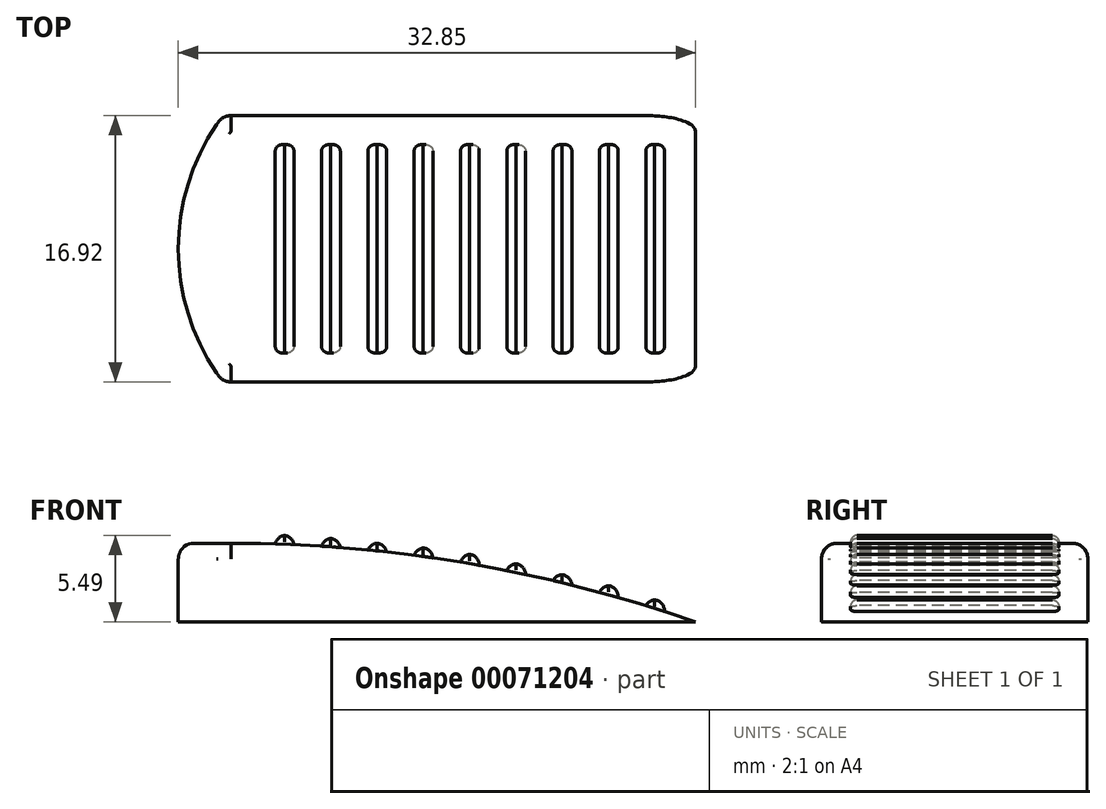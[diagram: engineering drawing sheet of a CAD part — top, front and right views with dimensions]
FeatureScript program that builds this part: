
annotation { "Feature Type Name" : "Feature", "Feature Type Description" : "" }
export const myFeature = defineFeature(function(context is Context, id is Id, definition is map)
    precondition{}
    {
        {
            var Q0;
            Q0=qCreatedBy(makeId("Top.planeOp"),FACE);
            var sketch = newSketch(context, id + "F0", { "sketchPlane" : qUnion([Q0])});
            skArc(sketch, "E0", {"start": v(11.65, 8.46) * mm, "mid": v(8.8, 0) * mm, "end": v(11.65, -8.46) * mm});
            skPoint(sketch, "E1.endSnap0", {"position": v(140.65, 0) * mm});
            skPoint(sketch, "E2.oppositeSnap0", {"position": v(24.14, -8.46) * mm});
            skLineSegment(sketch, "E2.bottom", {"start": v(11.65, 8.46) * mm, "end": v(41.65, 8.46) * mm});
            skLineSegment(sketch, "E2.top", {"start": v(11.65, -8.46) * mm, "end": v(41.65, -8.46) * mm});
            skLineSegment(sketch, "E2.right", {"start": v(41.65, 8.46) * mm, "end": v(41.65, -8.46) * mm});
            skSolve(sketch);
        }
        {
            var Q0;
            Q0=qSketchRegion(id+"F0",true);
            extrude(context, id + "F1", {"entities" : qUnion([Q0]), "depth" : 5 * mm});
        }
        {
            var Q0;
            Q0=makeQuery(id+"F1.opExtrude","CAP_EDGE",EDGE,{"disambiguationData":[OSD([sQuery(id+"F0.wireOp",EDGE,"E2.right")])],"isStart":false});
            fillet(context, id + "F2", {"entities" : qUnion([Q0]), "radius" : 90 * mm, "tangentPropagation" : true, "allowEdgeOverflow" : false});
        }
        {
            var Q0;
            Q0=makeQuery(id+"F2.opFillet","BLEND_EDGE",EDGE,{"blendedFrom":[makeQuery(id+"F1.opExtrude","CAP_EDGE",EDGE,{"disambiguationData":[OSD([sQuery(id+"F0.wireOp",EDGE,"E2.right")])],"isStart":false}),makeQuery(id+"F1.opExtrude","SWEPT_FACE",FACE,{"disambiguationData":[OSD([sQuery(id+"F0.wireOp",EDGE,"E2.top")])]})],"blendedInto":[makeQuery(id+"F1.opExtrude","SWEPT_FACE",FACE,{"disambiguationData":[OSD([sQuery(id+"F0.wireOp",EDGE,"E2.top")])]})]});
            var Q1;
            Q1=makeQuery(id+"F2.opFillet","BLEND_EDGE",EDGE,{"blendedFrom":[makeQuery(id+"F1.opExtrude","CAP_EDGE",EDGE,{"disambiguationData":[OSD([sQuery(id+"F0.wireOp",EDGE,"E2.right")])],"isStart":false}),makeQuery(id+"F1.opExtrude","SWEPT_FACE",FACE,{"disambiguationData":[OSD([sQuery(id+"F0.wireOp",EDGE,"E2.bottom")])]})],"blendedInto":[makeQuery(id+"F1.opExtrude","SWEPT_FACE",FACE,{"disambiguationData":[OSD([sQuery(id+"F0.wireOp",EDGE,"E2.bottom")])]})]});
            var Q2;
            Q2=makeQuery(id+"F1.opExtrude","CAP_EDGE",EDGE,{"disambiguationData":[OSD([sQuery(id+"F0.wireOp",EDGE,"E0")])],"isStart":false});
            fillet(context, id + "F3", {"entities" : qUnion([Q0, Q1, Q2]), "radius" : 1 * mm, "tangentPropagation" : true, "allowEdgeOverflow" : false});
        }
        {
            var Q0;
            Q0=makeQuery(id+"F1.opExtrude","SWEPT_EDGE",EDGE,{"disambiguationData":[OSD([sQuery(id+"F0.wireOp",EDGE,"E0"),sQuery(id+"F0.wireOp",EDGE,"E2.bottom")])]});
            var Q1;
            Q1=makeQuery(id+"F1.opExtrude","SWEPT_EDGE",EDGE,{"disambiguationData":[OSD([sQuery(id+"F0.wireOp",EDGE,"E0"),sQuery(id+"F0.wireOp",EDGE,"E2.top")])]});
            fillet(context, id + "F4", {"entities" : qUnion([Q0, Q1]), "radius" : 1 * mm, "tangentPropagation" : true, "allowEdgeOverflow" : false});
        }
        {
            var Q0;
            Q0=makeQuery(id+"F1.opExtrude","CAP_FACE",FACE,{"disambiguationData":[OSD([sQuery(id+"F0.wireOp",EDGE,"E0"),sQuery(id+"F0.wireOp",EDGE,"E2.bottom"),sQuery(id+"F0.wireOp",EDGE,"E2.top"),sQuery(id+"F0.wireOp",EDGE,"E2.right")])],"isStart":true});
            var sketch = newSketch(context, id + "F5", { "sketchPlane" : qUnion([Q0])});
            skPoint(sketch, "E3.rect.middle", {"position": v(27.32, 0) * mm});
            skPoint(sketch, "E4.startSnap0", {"position": v(21.43, 0) * mm});
            skPoint(sketch, "E5.startSnap0", {"position": v(18.5, 0) * mm});
            skPoint(sketch, "E6.rect.middle", {"position": v(15.55, 0) * mm});
            skLineSegment(sketch, "E7.rect.bottom", {"start": v(16.15, 6.61) * mm, "end": v(14.96, 6.61) * mm});
            skLineSegment(sketch, "E7.rect.top", {"start": v(16.15, -6.61) * mm, "end": v(14.96, -6.61) * mm});
            skLineSegment(sketch, "E7.rect.left", {"start": v(16.15, 6.61) * mm, "end": v(16.15, -6.61) * mm});
            skLineSegment(sketch, "E7.rect.right", {"start": v(14.96, 6.61) * mm, "end": v(14.96, -6.61) * mm});
            skLineSegment(sketch, "E8.MirrorCS", {"start": v(20.84, 6.61) * mm, "end": v(20.84, -6.61) * mm});
            skLineSegment(sketch, "E9.MirrorCS", {"start": v(22.03, 6.61) * mm, "end": v(22.03, -6.61) * mm});
            skLineSegment(sketch, "E10.MirrorCS", {"start": v(20.84, 6.61) * mm, "end": v(22.03, 6.61) * mm});
            skLineSegment(sketch, "E11.MirrorCS", {"start": v(20.84, -6.61) * mm, "end": v(22.03, -6.61) * mm});
            skLineSegment(sketch, "E12.MirrorCS", {"start": v(17.9, 6.61) * mm, "end": v(17.9, -6.61) * mm});
            skLineSegment(sketch, "E13.MirrorCS", {"start": v(19.09, 6.61) * mm, "end": v(19.09, -6.61) * mm});
            skLineSegment(sketch, "E14.MirrorCS", {"start": v(17.9, 6.61) * mm, "end": v(19.09, 6.61) * mm});
            skLineSegment(sketch, "E15.MirrorCS", {"start": v(17.9, -6.61) * mm, "end": v(19.09, -6.61) * mm});
            skLineSegment(sketch, "E16.MirrorCS", {"start": v(23.78, 6.61) * mm, "end": v(23.78, -6.61) * mm});
            skLineSegment(sketch, "E17.MirrorCS", {"start": v(24.97, 6.61) * mm, "end": v(24.97, -6.61) * mm});
            skLineSegment(sketch, "E18.MirrorCS", {"start": v(26.72, 6.61) * mm, "end": v(26.72, -6.61) * mm});
            skLineSegment(sketch, "E19.MirrorCS", {"start": v(27.91, 6.61) * mm, "end": v(27.91, -6.61) * mm});
            skLineSegment(sketch, "E20.MirrorCS", {"start": v(26.72, 6.61) * mm, "end": v(27.91, 6.61) * mm});
            skLineSegment(sketch, "E21.MirrorCS", {"start": v(26.72, -6.61) * mm, "end": v(27.91, -6.61) * mm});
            skLineSegment(sketch, "E22.MirrorCS", {"start": v(24.97, -6.61) * mm, "end": v(23.78, -6.61) * mm});
            skLineSegment(sketch, "E23.MirrorCS", {"start": v(24.97, 6.61) * mm, "end": v(23.78, 6.61) * mm});
            skLineSegment(sketch, "E24.MirrorCS", {"start": v(29.66, 6.61) * mm, "end": v(29.66, -6.61) * mm});
            skLineSegment(sketch, "E25.MirrorCS", {"start": v(30.85, 6.61) * mm, "end": v(30.85, -6.61) * mm});
            skLineSegment(sketch, "E26.MirrorCS", {"start": v(32.6, 6.61) * mm, "end": v(32.6, -6.61) * mm});
            skLineSegment(sketch, "E27.MirrorCS", {"start": v(33.8, 6.61) * mm, "end": v(33.8, -6.61) * mm});
            skLineSegment(sketch, "E28.MirrorCS", {"start": v(35.55, 6.61) * mm, "end": v(35.55, -6.61) * mm});
            skLineSegment(sketch, "E29.MirrorCS", {"start": v(36.74, 6.61) * mm, "end": v(36.74, -6.61) * mm});
            skLineSegment(sketch, "E30.MirrorCS", {"start": v(38.49, 6.61) * mm, "end": v(38.49, -6.61) * mm});
            skLineSegment(sketch, "E31.MirrorCS", {"start": v(39.68, 6.61) * mm, "end": v(39.68, -6.61) * mm});
            skLineSegment(sketch, "E32", {"start": v(29.66, 6.61) * mm, "end": v(30.85, 6.61) * mm});
            skLineSegment(sketch, "E33", {"start": v(32.6, 6.61) * mm, "end": v(33.8, 6.61) * mm});
            skLineSegment(sketch, "E34", {"start": v(35.55, 6.61) * mm, "end": v(36.74, 6.61) * mm});
            skLineSegment(sketch, "E35", {"start": v(38.49, 6.61) * mm, "end": v(39.68, 6.61) * mm});
            skLineSegment(sketch, "E36", {"start": v(39.68, -6.61) * mm, "end": v(38.49, -6.61) * mm});
            skLineSegment(sketch, "E37", {"start": v(36.74, -6.61) * mm, "end": v(35.55, -6.61) * mm});
            skLineSegment(sketch, "E38", {"start": v(33.8, -6.61) * mm, "end": v(32.6, -6.61) * mm});
            skLineSegment(sketch, "E39", {"start": v(30.85, -6.61) * mm, "end": v(29.66, -6.61) * mm});
            skSolve(sketch);
        }
        {
            var Q0;
            Q0=makeQuery(id+"F5.imprint","IMPRINT",FACE,{"disambiguationData":[TD([[makeQuery(id+"F5.imprint","IMPRINT",EDGE,{"derivedFrom":sQuery(id+"F5.wireOp",EDGE,"E7.rect.bottom")}),1.0]])]});
            extrude(context, id + "F6", {"entities" : qUnion([Q0]), "operationType" : NewBodyOperationType.ADD, "oppositeDirection" : true, "depth" : 5.5 * mm});
        }
        {
            var Q0;
            Q0=makeQuery(id+"F6.opExtrude","CAP_EDGE",EDGE,{"disambiguationData":[OSD([sQuery(id+"F5.wireOp",EDGE,"E7.rect.left")])],"isStart":false});
            var Q1;
            Q1=makeQuery(id+"F6.opExtrude","CAP_EDGE",EDGE,{"disambiguationData":[OSD([sQuery(id+"F5.wireOp",EDGE,"E7.rect.right")])],"isStart":false});
            fillet(context, id + "F7", {"entities" : qUnion([Q0, Q1]), "radius" : 0.7 * mm, "tangentPropagation" : true, "allowEdgeOverflow" : false});
        }
        {
            var Q0;
            Q0=makeQuery(id+"F5.imprint","IMPRINT",FACE,{"disambiguationData":[TD([[makeQuery(id+"F5.imprint","IMPRINT",EDGE,{"derivedFrom":sQuery(id+"F5.wireOp",EDGE,"E7.rect.bottom")}),-1.0]])]});
            var sketch = newSketch(context, id + "F8", { "sketchPlane" : qUnion([Q0])});
            skLineSegment(sketch, "E40.bottom", {"start": v(24.97, 6.61) * mm, "end": v(23.78, 6.61) * mm});
            skLineSegment(sketch, "E40.top", {"start": v(24.97, -6.61) * mm, "end": v(23.78, -6.61) * mm});
            skLineSegment(sketch, "E40.left", {"start": v(24.97, 6.61) * mm, "end": v(24.97, -6.61) * mm});
            skLineSegment(sketch, "E40.right", {"start": v(23.78, 6.61) * mm, "end": v(23.78, -6.61) * mm});
            skSolve(sketch);
        }
        {
            var Q0;
            Q0 = qSketchRegion(id + "F8", true);
            extrude(context, id + "F9", {"entities" : qUnion([Q0]), "operationType" : NewBodyOperationType.ADD, "oppositeDirection" : true, "depth" : 4.7 * mm});
        }
        {
            var Q0;
            Q0=makeQuery(id+"F9.opExtrude","CAP_EDGE",EDGE,{"disambiguationData":[OSD([sQuery(id+"F8.wireOp",EDGE,"E40.left")])],"isStart":false});
            var Q1;
            Q1=makeQuery(id+"F9.opExtrude","CAP_EDGE",EDGE,{"disambiguationData":[OSD([sQuery(id+"F8.wireOp",EDGE,"E40.right")])],"isStart":false});
            fillet(context, id + "F10", {"entities" : qUnion([Q0, Q1]), "radius" : 0.7 * mm, "tangentPropagation" : true, "allowEdgeOverflow" : false});
        }
        {
            var Q0;
            Q0=makeQuery(id+"F0.imprint","IMPRINT",FACE,{"disambiguationData":[TD([[makeQuery(id+"F0.imprint","IMPRINT",EDGE,{"derivedFrom":sQuery(id+"F0.wireOp",EDGE,"E0")}),1.0]])]});
            var sketch = newSketch(context, id + "F11", { "sketchPlane" : qUnion([Q0])});
            skLineSegment(sketch, "E41.bottom", {"start": v(33.8, -6.61) * mm, "end": v(32.6, -6.61) * mm});
            skLineSegment(sketch, "E41.top", {"start": v(33.8, 6.61) * mm, "end": v(32.6, 6.61) * mm});
            skLineSegment(sketch, "E41.left", {"start": v(33.8, -6.61) * mm, "end": v(33.8, 6.61) * mm});
            skLineSegment(sketch, "E41.right", {"start": v(32.6, -6.61) * mm, "end": v(32.6, 6.61) * mm});
            skSolve(sketch);
        }
        {
            var Q0;
            Q0=makeQuery(id+"F11.imprint","IMPRINT",FACE,{"disambiguationData":[TD([[makeQuery(id+"F11.imprint","IMPRINT",EDGE,{"derivedFrom":sQuery(id+"F11.wireOp",EDGE,"E41.bottom")}),-1.0]])]});
            extrude(context, id + "F12", {"entities" : qUnion([Q0]), "operationType" : NewBodyOperationType.ADD, "depth" : 3 * mm});
        }
        {
            var Q0;
            Q0=makeQuery(id+"F12.opExtrude","CAP_EDGE",EDGE,{"disambiguationData":[OSD([sQuery(id+"F11.wireOp",EDGE,"E41.left")])],"isStart":false});
            var Q1;
            Q1=makeQuery(id+"F12.opExtrude","CAP_EDGE",EDGE,{"disambiguationData":[OSD([sQuery(id+"F11.wireOp",EDGE,"E41.right")])],"isStart":false});
            fillet(context, id + "F13", {"entities" : qUnion([Q0, Q1]), "radius" : 0.7 * mm, "tangentPropagation" : true, "allowEdgeOverflow" : false});
        }
        {
            var Q0;
            Q0=makeQuery(id+"F5.imprint","IMPRINT",FACE,{"disambiguationData":[TD([[makeQuery(id+"F5.imprint","IMPRINT",EDGE,{"derivedFrom":sQuery(id+"F5.wireOp",EDGE,"E7.rect.bottom")}),-1.0]])]});
            var sketch = newSketch(context, id + "F14", { "sketchPlane" : qUnion([Q0])});
            skLineSegment(sketch, "E42.bottom", {"start": v(39.68, 6.61) * mm, "end": v(38.49, 6.61) * mm});
            skLineSegment(sketch, "E42.top", {"start": v(39.68, -6.61) * mm, "end": v(38.49, -6.61) * mm});
            skLineSegment(sketch, "E42.left", {"start": v(39.68, 6.61) * mm, "end": v(39.68, -6.61) * mm});
            skLineSegment(sketch, "E42.right", {"start": v(38.49, 6.61) * mm, "end": v(38.49, -6.61) * mm});
            skSolve(sketch);
        }
        {
            var Q0;
            Q0 = qSketchRegion(id + "F14", true);
            extrude(context, id + "F15", {"entities" : qUnion([Q0]), "operationType" : NewBodyOperationType.ADD, "oppositeDirection" : true, "depth" : 1.4 * mm});
        }
        {
            var Q0;
            Q0=makeQuery(id+"F15.opExtrude","CAP_EDGE",EDGE,{"disambiguationData":[OSD([sQuery(id+"F14.wireOp",EDGE,"E42.right")])],"isStart":false});
            var Q1;
            Q1=makeQuery(id+"F15.opExtrude","CAP_EDGE",EDGE,{"disambiguationData":[OSD([sQuery(id+"F14.wireOp",EDGE,"E42.left")])],"isStart":false});
            fillet(context, id + "F16", {"entities" : qUnion([Q0, Q1]), "radius" : 0.7 * mm, "tangentPropagation" : true, "allowEdgeOverflow" : false});
        }
        {
            var Q0;
            Q0=makeQuery(id+"F0.imprint","IMPRINT",FACE,{"disambiguationData":[TD([[makeQuery(id+"F0.imprint","IMPRINT",EDGE,{"derivedFrom":sQuery(id+"F0.wireOp",EDGE,"E0")}),1.0]])]});
            var sketch = newSketch(context, id + "F17", { "sketchPlane" : qUnion([Q0])});
            skLineSegment(sketch, "E43.bottom", {"start": v(35.55, -6.61) * mm, "end": v(36.74, -6.61) * mm});
            skLineSegment(sketch, "E43.top", {"start": v(35.55, 6.61) * mm, "end": v(36.74, 6.61) * mm});
            skLineSegment(sketch, "E43.left", {"start": v(35.55, -6.61) * mm, "end": v(35.55, 6.61) * mm});
            skLineSegment(sketch, "E43.right", {"start": v(36.74, -6.61) * mm, "end": v(36.74, 6.61) * mm});
            skSolve(sketch);
        }
        {
            var Q0;
            Q0 = qSketchRegion(id + "F17", true);
            extrude(context, id + "F18", {"entities" : qUnion([Q0]), "operationType" : NewBodyOperationType.ADD, "depth" : 2.3 * mm});
        }
        {
            var Q0;
            Q0=makeQuery(id+"F18.opExtrude","CAP_EDGE",EDGE,{"disambiguationData":[OSD([sQuery(id+"F17.wireOp",EDGE,"E43.left")])],"isStart":false});
            var Q1;
            Q1=makeQuery(id+"F18.opExtrude","CAP_EDGE",EDGE,{"disambiguationData":[OSD([sQuery(id+"F17.wireOp",EDGE,"E43.right")])],"isStart":false});
            fillet(context, id + "F19", {"entities" : qUnion([Q0, Q1]), "radius" : 0.7 * mm, "tangentPropagation" : true, "allowEdgeOverflow" : false});
        }
        {
            var Q0;
            Q0=makeQuery(id+"F0.imprint","IMPRINT",FACE,{"disambiguationData":[TD([[makeQuery(id+"F0.imprint","IMPRINT",EDGE,{"derivedFrom":sQuery(id+"F0.wireOp",EDGE,"E0")}),1.0]])]});
            var sketch = newSketch(context, id + "F20", { "sketchPlane" : qUnion([Q0])});
            skLineSegment(sketch, "E44.bottom", {"start": v(30.85, -6.61) * mm, "end": v(29.66, -6.61) * mm});
            skLineSegment(sketch, "E44.top", {"start": v(30.85, 6.61) * mm, "end": v(29.66, 6.61) * mm});
            skLineSegment(sketch, "E44.left", {"start": v(30.85, -6.61) * mm, "end": v(30.85, 6.61) * mm});
            skLineSegment(sketch, "E44.right", {"start": v(29.66, -6.61) * mm, "end": v(29.66, 6.61) * mm});
            skSolve(sketch);
        }
        {
            var Q0;
            Q0 = qSketchRegion(id + "F20", true);
            extrude(context, id + "F21", {"entities" : qUnion([Q0]), "operationType" : NewBodyOperationType.ADD, "depth" : 3.7 * mm});
        }
        {
            var Q0;
            Q0=makeQuery(id+"F21.opExtrude","CAP_EDGE",EDGE,{"disambiguationData":[OSD([sQuery(id+"F20.wireOp",EDGE,"E44.right")])],"isStart":false});
            var Q1;
            Q1=makeQuery(id+"F21.opExtrude","CAP_EDGE",EDGE,{"disambiguationData":[OSD([sQuery(id+"F20.wireOp",EDGE,"E44.left")])],"isStart":false});
            fillet(context, id + "F22", {"entities" : qUnion([Q0, Q1]), "radius" : 0.7 * mm, "tangentPropagation" : true, "allowEdgeOverflow" : false});
        }
        {
            var Q0;
            Q0=makeQuery(id+"F0.imprint","IMPRINT",FACE,{"disambiguationData":[TD([[makeQuery(id+"F0.imprint","IMPRINT",EDGE,{"derivedFrom":sQuery(id+"F0.wireOp",EDGE,"E0")}),1.0]])]});
            var sketch = newSketch(context, id + "F23", { "sketchPlane" : qUnion([Q0])});
            skLineSegment(sketch, "E45.bottom", {"start": v(27.91, -6.61) * mm, "end": v(26.72, -6.61) * mm});
            skLineSegment(sketch, "E45.top", {"start": v(27.91, 6.61) * mm, "end": v(26.72, 6.61) * mm});
            skLineSegment(sketch, "E45.left", {"start": v(27.91, -6.61) * mm, "end": v(27.91, 6.61) * mm});
            skLineSegment(sketch, "E45.right", {"start": v(26.72, -6.61) * mm, "end": v(26.72, 6.61) * mm});
            skSolve(sketch);
        }
        {
            var Q0;
            Q0 = qSketchRegion(id + "F23", true);
            extrude(context, id + "F24", {"entities" : qUnion([Q0]), "operationType" : NewBodyOperationType.ADD, "depth" : 4.3 * mm});
        }
        {
            var Q0;
            Q0=makeQuery(id+"F24.opExtrude","CAP_EDGE",EDGE,{"disambiguationData":[OSD([sQuery(id+"F23.wireOp",EDGE,"E45.right")])],"isStart":false});
            var Q1;
            Q1=makeQuery(id+"F24.opExtrude","CAP_EDGE",EDGE,{"disambiguationData":[OSD([sQuery(id+"F23.wireOp",EDGE,"E45.left")])],"isStart":false});
            fillet(context, id + "F25", {"entities" : qUnion([Q0, Q1]), "radius" : 0.7 * mm, "tangentPropagation" : true, "allowEdgeOverflow" : false});
        }
        {
            var Q0;
            Q0=makeQuery(id+"F5.imprint","IMPRINT",FACE,{"disambiguationData":[TD([[makeQuery(id+"F5.imprint","IMPRINT",EDGE,{"derivedFrom":sQuery(id+"F5.wireOp",EDGE,"E7.rect.bottom")}),-1.0]])]});
            var sketch = newSketch(context, id + "F26", { "sketchPlane" : qUnion([Q0])});
            skLineSegment(sketch, "E46.bottom", {"start": v(17.9, 6.61) * mm, "end": v(19.09, 6.61) * mm});
            skLineSegment(sketch, "E46.top", {"start": v(17.9, -6.61) * mm, "end": v(19.09, -6.61) * mm});
            skLineSegment(sketch, "E46.left", {"start": v(17.9, 6.61) * mm, "end": v(17.9, -6.61) * mm});
            skLineSegment(sketch, "E46.right", {"start": v(19.09, 6.61) * mm, "end": v(19.09, -6.61) * mm});
            skSolve(sketch);
        }
        {
            var Q0;
            Q0 = qSketchRegion(id + "F26", true);
            extrude(context, id + "F27", {"entities" : qUnion([Q0]), "operationType" : NewBodyOperationType.ADD, "oppositeDirection" : true, "depth" : 5.3 * mm});
        }
        {
            var Q0;
            Q0=makeQuery(id+"F27.opExtrude","CAP_EDGE",EDGE,{"disambiguationData":[OSD([sQuery(id+"F26.wireOp",EDGE,"E46.left")])],"isStart":false});
            var Q1;
            Q1=makeQuery(id+"F27.opExtrude","CAP_EDGE",EDGE,{"disambiguationData":[OSD([sQuery(id+"F26.wireOp",EDGE,"E46.right")])],"isStart":false});
            fillet(context, id + "F28", {"entities" : qUnion([Q0, Q1]), "radius" : 0.7 * mm, "tangentPropagation" : true, "allowEdgeOverflow" : false});
        }
        {
            var Q0;
            Q0=makeQuery(id+"F0.imprint","IMPRINT",FACE,{"disambiguationData":[TD([[makeQuery(id+"F0.imprint","IMPRINT",EDGE,{"derivedFrom":sQuery(id+"F0.wireOp",EDGE,"E0")}),1.0]])]});
            var sketch = newSketch(context, id + "F29", { "sketchPlane" : qUnion([Q0])});
            skLineSegment(sketch, "E47.bottom", {"start": v(22.03, -6.61) * mm, "end": v(20.84, -6.61) * mm});
            skLineSegment(sketch, "E47.top", {"start": v(22.03, 6.61) * mm, "end": v(20.84, 6.61) * mm});
            skLineSegment(sketch, "E47.left", {"start": v(22.03, -6.61) * mm, "end": v(22.03, 6.61) * mm});
            skLineSegment(sketch, "E47.right", {"start": v(20.84, -6.61) * mm, "end": v(20.84, 6.61) * mm});
            skSolve(sketch);
        }
        {
            var Q0;
            Q0 = qSketchRegion(id + "F29", true);
            extrude(context, id + "F30", {"entities" : qUnion([Q0]), "operationType" : NewBodyOperationType.ADD, "depth" : 5 * mm});
        }
        {
            var Q0;
            Q0=makeQuery(id+"F30.opExtrude","CAP_EDGE",EDGE,{"disambiguationData":[OSD([sQuery(id+"F29.wireOp",EDGE,"E47.right")])],"isStart":false});
            var Q1;
            Q1=makeQuery(id+"F30.opExtrude","CAP_EDGE",EDGE,{"disambiguationData":[OSD([sQuery(id+"F29.wireOp",EDGE,"E47.left")])],"isStart":false});
            fillet(context, id + "F31", {"entities" : qUnion([Q0, Q1]), "radius" : 0.7 * mm, "tangentPropagation" : true, "allowEdgeOverflow" : false});
        }
        {
            var Q0;
            Q0=makeQuery(id+"F7.opFillet","BLEND_EDGE",EDGE,{"blendedFrom":[makeQuery(id+"F6.opExtrude","CAP_EDGE",EDGE,{"disambiguationData":[OSD([sQuery(id+"F5.wireOp",EDGE,"E7.rect.left")])],"isStart":false}),makeQuery(id+"F6.opExtrude","SWEPT_FACE",FACE,{"disambiguationData":[OSD([sQuery(id+"F5.wireOp",EDGE,"E7.rect.bottom")])]})],"blendedInto":[makeQuery(id+"F6.opExtrude","SWEPT_FACE",FACE,{"disambiguationData":[OSD([sQuery(id+"F5.wireOp",EDGE,"E7.rect.bottom")])]})]});
            var Q1;
            Q1=makeQuery(id+"F7.opFillet","BLEND_EDGE",EDGE,{"blendedFrom":[makeQuery(id+"F6.opExtrude","CAP_EDGE",EDGE,{"disambiguationData":[OSD([sQuery(id+"F5.wireOp",EDGE,"E7.rect.right")])],"isStart":false}),makeQuery(id+"F6.opExtrude","SWEPT_FACE",FACE,{"disambiguationData":[OSD([sQuery(id+"F5.wireOp",EDGE,"E7.rect.bottom")])]})],"blendedInto":[makeQuery(id+"F6.opExtrude","SWEPT_FACE",FACE,{"disambiguationData":[OSD([sQuery(id+"F5.wireOp",EDGE,"E7.rect.bottom")])]})]});
            var Q2;
            Q2=makeQuery(id+"F28.opFillet","BLEND_EDGE",EDGE,{"blendedFrom":[makeQuery(id+"F27.opExtrude","CAP_EDGE",EDGE,{"disambiguationData":[OSD([sQuery(id+"F26.wireOp",EDGE,"E46.left")])],"isStart":false}),makeQuery(id+"F27.opExtrude","SWEPT_FACE",FACE,{"disambiguationData":[OSD([sQuery(id+"F26.wireOp",EDGE,"E46.bottom")])]})],"blendedInto":[makeQuery(id+"F27.opExtrude","SWEPT_FACE",FACE,{"disambiguationData":[OSD([sQuery(id+"F26.wireOp",EDGE,"E46.bottom")])]})]});
            var Q3;
            Q3=makeQuery(id+"F28.opFillet","BLEND_EDGE",EDGE,{"blendedFrom":[makeQuery(id+"F27.opExtrude","CAP_EDGE",EDGE,{"disambiguationData":[OSD([sQuery(id+"F26.wireOp",EDGE,"E46.right")])],"isStart":false}),makeQuery(id+"F27.opExtrude","SWEPT_FACE",FACE,{"disambiguationData":[OSD([sQuery(id+"F26.wireOp",EDGE,"E46.bottom")])]})],"blendedInto":[makeQuery(id+"F27.opExtrude","SWEPT_FACE",FACE,{"disambiguationData":[OSD([sQuery(id+"F26.wireOp",EDGE,"E46.bottom")])]})]});
            var Q4;
            Q4=makeQuery(id+"F31.opFillet","BLEND_EDGE",EDGE,{"blendedFrom":[makeQuery(id+"F30.opExtrude","CAP_EDGE",EDGE,{"disambiguationData":[OSD([sQuery(id+"F29.wireOp",EDGE,"E47.right")])],"isStart":false}),makeQuery(id+"F30.opExtrude","SWEPT_FACE",FACE,{"disambiguationData":[OSD([sQuery(id+"F29.wireOp",EDGE,"E47.bottom")])]})],"blendedInto":[makeQuery(id+"F30.opExtrude","SWEPT_FACE",FACE,{"disambiguationData":[OSD([sQuery(id+"F29.wireOp",EDGE,"E47.bottom")])]})]});
            var Q5;
            Q5=makeQuery(id+"F31.opFillet","BLEND_EDGE",EDGE,{"blendedFrom":[makeQuery(id+"F30.opExtrude","CAP_EDGE",EDGE,{"disambiguationData":[OSD([sQuery(id+"F29.wireOp",EDGE,"E47.left")])],"isStart":false}),makeQuery(id+"F30.opExtrude","SWEPT_FACE",FACE,{"disambiguationData":[OSD([sQuery(id+"F29.wireOp",EDGE,"E47.bottom")])]})],"blendedInto":[makeQuery(id+"F30.opExtrude","SWEPT_FACE",FACE,{"disambiguationData":[OSD([sQuery(id+"F29.wireOp",EDGE,"E47.bottom")])]})]});
            var Q6;
            Q6=makeQuery(id+"F10.opFillet","BLEND_EDGE",EDGE,{"blendedFrom":[makeQuery(id+"F9.opExtrude","CAP_EDGE",EDGE,{"disambiguationData":[OSD([sQuery(id+"F8.wireOp",EDGE,"E40.right")])],"isStart":false}),makeQuery(id+"F9.opExtrude","SWEPT_FACE",FACE,{"disambiguationData":[OSD([sQuery(id+"F8.wireOp",EDGE,"E40.bottom")])]})],"blendedInto":[makeQuery(id+"F9.opExtrude","SWEPT_FACE",FACE,{"disambiguationData":[OSD([sQuery(id+"F8.wireOp",EDGE,"E40.bottom")])]})]});
            var Q7;
            Q7=makeQuery(id+"F10.opFillet","BLEND_EDGE",EDGE,{"blendedFrom":[makeQuery(id+"F9.opExtrude","CAP_EDGE",EDGE,{"disambiguationData":[OSD([sQuery(id+"F8.wireOp",EDGE,"E40.left")])],"isStart":false}),makeQuery(id+"F9.opExtrude","SWEPT_FACE",FACE,{"disambiguationData":[OSD([sQuery(id+"F8.wireOp",EDGE,"E40.bottom")])]})],"blendedInto":[makeQuery(id+"F9.opExtrude","SWEPT_FACE",FACE,{"disambiguationData":[OSD([sQuery(id+"F8.wireOp",EDGE,"E40.bottom")])]})]});
            var Q8;
            Q8=makeQuery(id+"F25.opFillet","BLEND_EDGE",EDGE,{"blendedFrom":[makeQuery(id+"F24.opExtrude","CAP_EDGE",EDGE,{"disambiguationData":[OSD([sQuery(id+"F23.wireOp",EDGE,"E45.right")])],"isStart":false}),makeQuery(id+"F24.opExtrude","SWEPT_FACE",FACE,{"disambiguationData":[OSD([sQuery(id+"F23.wireOp",EDGE,"E45.bottom")])]})],"blendedInto":[makeQuery(id+"F24.opExtrude","SWEPT_FACE",FACE,{"disambiguationData":[OSD([sQuery(id+"F23.wireOp",EDGE,"E45.bottom")])]})]});
            var Q9;
            Q9=makeQuery(id+"F25.opFillet","BLEND_EDGE",EDGE,{"blendedFrom":[makeQuery(id+"F24.opExtrude","CAP_EDGE",EDGE,{"disambiguationData":[OSD([sQuery(id+"F23.wireOp",EDGE,"E45.left")])],"isStart":false}),makeQuery(id+"F24.opExtrude","SWEPT_FACE",FACE,{"disambiguationData":[OSD([sQuery(id+"F23.wireOp",EDGE,"E45.bottom")])]})],"blendedInto":[makeQuery(id+"F24.opExtrude","SWEPT_FACE",FACE,{"disambiguationData":[OSD([sQuery(id+"F23.wireOp",EDGE,"E45.bottom")])]})]});
            var Q10;
            Q10=makeQuery(id+"F22.opFillet","BLEND_EDGE",EDGE,{"blendedFrom":[makeQuery(id+"F21.opExtrude","CAP_EDGE",EDGE,{"disambiguationData":[OSD([sQuery(id+"F20.wireOp",EDGE,"E44.right")])],"isStart":false}),makeQuery(id+"F21.opExtrude","SWEPT_FACE",FACE,{"disambiguationData":[OSD([sQuery(id+"F20.wireOp",EDGE,"E44.bottom")])]})],"blendedInto":[makeQuery(id+"F21.opExtrude","SWEPT_FACE",FACE,{"disambiguationData":[OSD([sQuery(id+"F20.wireOp",EDGE,"E44.bottom")])]})]});
            var Q11;
            Q11=makeQuery(id+"F22.opFillet","BLEND_EDGE",EDGE,{"blendedFrom":[makeQuery(id+"F21.opExtrude","CAP_EDGE",EDGE,{"disambiguationData":[OSD([sQuery(id+"F20.wireOp",EDGE,"E44.left")])],"isStart":false}),makeQuery(id+"F21.opExtrude","SWEPT_FACE",FACE,{"disambiguationData":[OSD([sQuery(id+"F20.wireOp",EDGE,"E44.bottom")])]})],"blendedInto":[makeQuery(id+"F21.opExtrude","SWEPT_FACE",FACE,{"disambiguationData":[OSD([sQuery(id+"F20.wireOp",EDGE,"E44.bottom")])]})]});
            var Q12;
            Q12=makeQuery(id+"F13.opFillet","BLEND_EDGE",EDGE,{"blendedFrom":[makeQuery(id+"F12.opExtrude","CAP_EDGE",EDGE,{"disambiguationData":[OSD([sQuery(id+"F11.wireOp",EDGE,"E41.right")])],"isStart":false}),makeQuery(id+"F12.opExtrude","SWEPT_FACE",FACE,{"disambiguationData":[OSD([sQuery(id+"F11.wireOp",EDGE,"E41.bottom")])]})],"blendedInto":[makeQuery(id+"F12.opExtrude","SWEPT_FACE",FACE,{"disambiguationData":[OSD([sQuery(id+"F11.wireOp",EDGE,"E41.bottom")])]})]});
            var Q13;
            Q13=makeQuery(id+"F13.opFillet","BLEND_EDGE",EDGE,{"blendedFrom":[makeQuery(id+"F12.opExtrude","CAP_EDGE",EDGE,{"disambiguationData":[OSD([sQuery(id+"F11.wireOp",EDGE,"E41.left")])],"isStart":false}),makeQuery(id+"F12.opExtrude","SWEPT_FACE",FACE,{"disambiguationData":[OSD([sQuery(id+"F11.wireOp",EDGE,"E41.bottom")])]})],"blendedInto":[makeQuery(id+"F12.opExtrude","SWEPT_FACE",FACE,{"disambiguationData":[OSD([sQuery(id+"F11.wireOp",EDGE,"E41.bottom")])]})]});
            var Q14;
            Q14=makeQuery(id+"F19.opFillet","BLEND_EDGE",EDGE,{"blendedFrom":[makeQuery(id+"F18.opExtrude","CAP_EDGE",EDGE,{"disambiguationData":[OSD([sQuery(id+"F17.wireOp",EDGE,"E43.left")])],"isStart":false}),makeQuery(id+"F18.opExtrude","SWEPT_FACE",FACE,{"disambiguationData":[OSD([sQuery(id+"F17.wireOp",EDGE,"E43.bottom")])]})],"blendedInto":[makeQuery(id+"F18.opExtrude","SWEPT_FACE",FACE,{"disambiguationData":[OSD([sQuery(id+"F17.wireOp",EDGE,"E43.bottom")])]})]});
            var Q15;
            Q15=makeQuery(id+"F19.opFillet","BLEND_EDGE",EDGE,{"blendedFrom":[makeQuery(id+"F18.opExtrude","CAP_EDGE",EDGE,{"disambiguationData":[OSD([sQuery(id+"F17.wireOp",EDGE,"E43.right")])],"isStart":false}),makeQuery(id+"F18.opExtrude","SWEPT_FACE",FACE,{"disambiguationData":[OSD([sQuery(id+"F17.wireOp",EDGE,"E43.bottom")])]})],"blendedInto":[makeQuery(id+"F18.opExtrude","SWEPT_FACE",FACE,{"disambiguationData":[OSD([sQuery(id+"F17.wireOp",EDGE,"E43.bottom")])]})]});
            var Q16;
            Q16=makeQuery(id+"F16.opFillet","BLEND_EDGE",EDGE,{"blendedFrom":[makeQuery(id+"F15.opExtrude","CAP_EDGE",EDGE,{"disambiguationData":[OSD([sQuery(id+"F14.wireOp",EDGE,"E42.right")])],"isStart":false}),makeQuery(id+"F15.opExtrude","SWEPT_FACE",FACE,{"disambiguationData":[OSD([sQuery(id+"F14.wireOp",EDGE,"E42.bottom")])]})],"blendedInto":[makeQuery(id+"F15.opExtrude","SWEPT_FACE",FACE,{"disambiguationData":[OSD([sQuery(id+"F14.wireOp",EDGE,"E42.bottom")])]})]});
            var Q17;
            Q17=makeQuery(id+"F16.opFillet","BLEND_EDGE",EDGE,{"blendedFrom":[makeQuery(id+"F15.opExtrude","CAP_EDGE",EDGE,{"disambiguationData":[OSD([sQuery(id+"F14.wireOp",EDGE,"E42.left")])],"isStart":false}),makeQuery(id+"F15.opExtrude","SWEPT_FACE",FACE,{"disambiguationData":[OSD([sQuery(id+"F14.wireOp",EDGE,"E42.bottom")])]})],"blendedInto":[makeQuery(id+"F15.opExtrude","SWEPT_FACE",FACE,{"disambiguationData":[OSD([sQuery(id+"F14.wireOp",EDGE,"E42.bottom")])]})]});
            var Q18;
            Q18=makeQuery(id+"F16.opFillet","BLEND_EDGE",EDGE,{"blendedFrom":[makeQuery(id+"F15.opExtrude","CAP_EDGE",EDGE,{"disambiguationData":[OSD([sQuery(id+"F14.wireOp",EDGE,"E42.right")])],"isStart":false}),makeQuery(id+"F15.opExtrude","SWEPT_FACE",FACE,{"disambiguationData":[OSD([sQuery(id+"F14.wireOp",EDGE,"E42.top")])]})],"blendedInto":[makeQuery(id+"F15.opExtrude","SWEPT_FACE",FACE,{"disambiguationData":[OSD([sQuery(id+"F14.wireOp",EDGE,"E42.top")])]})]});
            var Q19;
            Q19=makeQuery(id+"F16.opFillet","BLEND_EDGE",EDGE,{"blendedFrom":[makeQuery(id+"F15.opExtrude","CAP_EDGE",EDGE,{"disambiguationData":[OSD([sQuery(id+"F14.wireOp",EDGE,"E42.left")])],"isStart":false}),makeQuery(id+"F15.opExtrude","SWEPT_FACE",FACE,{"disambiguationData":[OSD([sQuery(id+"F14.wireOp",EDGE,"E42.top")])]})],"blendedInto":[makeQuery(id+"F15.opExtrude","SWEPT_FACE",FACE,{"disambiguationData":[OSD([sQuery(id+"F14.wireOp",EDGE,"E42.top")])]})]});
            var Q20;
            Q20=makeQuery(id+"F19.opFillet","BLEND_EDGE",EDGE,{"blendedFrom":[makeQuery(id+"F18.opExtrude","CAP_EDGE",EDGE,{"disambiguationData":[OSD([sQuery(id+"F17.wireOp",EDGE,"E43.right")])],"isStart":false}),makeQuery(id+"F18.opExtrude","SWEPT_FACE",FACE,{"disambiguationData":[OSD([sQuery(id+"F17.wireOp",EDGE,"E43.top")])]})],"blendedInto":[makeQuery(id+"F18.opExtrude","SWEPT_FACE",FACE,{"disambiguationData":[OSD([sQuery(id+"F17.wireOp",EDGE,"E43.top")])]})]});
            var Q21;
            Q21=makeQuery(id+"F19.opFillet","BLEND_EDGE",EDGE,{"blendedFrom":[makeQuery(id+"F18.opExtrude","CAP_EDGE",EDGE,{"disambiguationData":[OSD([sQuery(id+"F17.wireOp",EDGE,"E43.left")])],"isStart":false}),makeQuery(id+"F18.opExtrude","SWEPT_FACE",FACE,{"disambiguationData":[OSD([sQuery(id+"F17.wireOp",EDGE,"E43.top")])]})],"blendedInto":[makeQuery(id+"F18.opExtrude","SWEPT_FACE",FACE,{"disambiguationData":[OSD([sQuery(id+"F17.wireOp",EDGE,"E43.top")])]})]});
            var Q22;
            Q22=makeQuery(id+"F7.opFillet","BLEND_EDGE",EDGE,{"blendedFrom":[makeQuery(id+"F6.opExtrude","CAP_EDGE",EDGE,{"disambiguationData":[OSD([sQuery(id+"F5.wireOp",EDGE,"E7.rect.right")])],"isStart":false}),makeQuery(id+"F6.opExtrude","SWEPT_FACE",FACE,{"disambiguationData":[OSD([sQuery(id+"F5.wireOp",EDGE,"E7.rect.top")])]})],"blendedInto":[makeQuery(id+"F6.opExtrude","SWEPT_FACE",FACE,{"disambiguationData":[OSD([sQuery(id+"F5.wireOp",EDGE,"E7.rect.top")])]})]});
            var Q23;
            Q23=makeQuery(id+"F7.opFillet","BLEND_EDGE",EDGE,{"blendedFrom":[makeQuery(id+"F6.opExtrude","CAP_EDGE",EDGE,{"disambiguationData":[OSD([sQuery(id+"F5.wireOp",EDGE,"E7.rect.left")])],"isStart":false}),makeQuery(id+"F6.opExtrude","SWEPT_FACE",FACE,{"disambiguationData":[OSD([sQuery(id+"F5.wireOp",EDGE,"E7.rect.top")])]})],"blendedInto":[makeQuery(id+"F6.opExtrude","SWEPT_FACE",FACE,{"disambiguationData":[OSD([sQuery(id+"F5.wireOp",EDGE,"E7.rect.top")])]})]});
            var Q24;
            Q24=makeQuery(id+"F28.opFillet","BLEND_EDGE",EDGE,{"blendedFrom":[makeQuery(id+"F27.opExtrude","CAP_EDGE",EDGE,{"disambiguationData":[OSD([sQuery(id+"F26.wireOp",EDGE,"E46.left")])],"isStart":false}),makeQuery(id+"F27.opExtrude","SWEPT_FACE",FACE,{"disambiguationData":[OSD([sQuery(id+"F26.wireOp",EDGE,"E46.top")])]})],"blendedInto":[makeQuery(id+"F27.opExtrude","SWEPT_FACE",FACE,{"disambiguationData":[OSD([sQuery(id+"F26.wireOp",EDGE,"E46.top")])]})]});
            var Q25;
            Q25=makeQuery(id+"F28.opFillet","BLEND_EDGE",EDGE,{"blendedFrom":[makeQuery(id+"F27.opExtrude","CAP_EDGE",EDGE,{"disambiguationData":[OSD([sQuery(id+"F26.wireOp",EDGE,"E46.right")])],"isStart":false}),makeQuery(id+"F27.opExtrude","SWEPT_FACE",FACE,{"disambiguationData":[OSD([sQuery(id+"F26.wireOp",EDGE,"E46.top")])]})],"blendedInto":[makeQuery(id+"F27.opExtrude","SWEPT_FACE",FACE,{"disambiguationData":[OSD([sQuery(id+"F26.wireOp",EDGE,"E46.top")])]})]});
            var Q26;
            Q26=makeQuery(id+"F31.opFillet","BLEND_EDGE",EDGE,{"blendedFrom":[makeQuery(id+"F30.opExtrude","CAP_EDGE",EDGE,{"disambiguationData":[OSD([sQuery(id+"F29.wireOp",EDGE,"E47.right")])],"isStart":false}),makeQuery(id+"F30.opExtrude","SWEPT_FACE",FACE,{"disambiguationData":[OSD([sQuery(id+"F29.wireOp",EDGE,"E47.top")])]})],"blendedInto":[makeQuery(id+"F30.opExtrude","SWEPT_FACE",FACE,{"disambiguationData":[OSD([sQuery(id+"F29.wireOp",EDGE,"E47.top")])]})]});
            var Q27;
            Q27=makeQuery(id+"F31.opFillet","BLEND_EDGE",EDGE,{"blendedFrom":[makeQuery(id+"F30.opExtrude","CAP_EDGE",EDGE,{"disambiguationData":[OSD([sQuery(id+"F29.wireOp",EDGE,"E47.left")])],"isStart":false}),makeQuery(id+"F30.opExtrude","SWEPT_FACE",FACE,{"disambiguationData":[OSD([sQuery(id+"F29.wireOp",EDGE,"E47.top")])]})],"blendedInto":[makeQuery(id+"F30.opExtrude","SWEPT_FACE",FACE,{"disambiguationData":[OSD([sQuery(id+"F29.wireOp",EDGE,"E47.top")])]})]});
            var Q28;
            Q28=makeQuery(id+"F10.opFillet","BLEND_EDGE",EDGE,{"blendedFrom":[makeQuery(id+"F9.opExtrude","CAP_EDGE",EDGE,{"disambiguationData":[OSD([sQuery(id+"F8.wireOp",EDGE,"E40.right")])],"isStart":false}),makeQuery(id+"F9.opExtrude","SWEPT_FACE",FACE,{"disambiguationData":[OSD([sQuery(id+"F8.wireOp",EDGE,"E40.top")])]})],"blendedInto":[makeQuery(id+"F9.opExtrude","SWEPT_FACE",FACE,{"disambiguationData":[OSD([sQuery(id+"F8.wireOp",EDGE,"E40.top")])]})]});
            var Q29;
            Q29=makeQuery(id+"F10.opFillet","BLEND_EDGE",EDGE,{"blendedFrom":[makeQuery(id+"F9.opExtrude","CAP_EDGE",EDGE,{"disambiguationData":[OSD([sQuery(id+"F8.wireOp",EDGE,"E40.left")])],"isStart":false}),makeQuery(id+"F9.opExtrude","SWEPT_FACE",FACE,{"disambiguationData":[OSD([sQuery(id+"F8.wireOp",EDGE,"E40.top")])]})],"blendedInto":[makeQuery(id+"F9.opExtrude","SWEPT_FACE",FACE,{"disambiguationData":[OSD([sQuery(id+"F8.wireOp",EDGE,"E40.top")])]})]});
            var Q30;
            Q30=makeQuery(id+"F25.opFillet","BLEND_EDGE",EDGE,{"blendedFrom":[makeQuery(id+"F24.opExtrude","CAP_EDGE",EDGE,{"disambiguationData":[OSD([sQuery(id+"F23.wireOp",EDGE,"E45.right")])],"isStart":false}),makeQuery(id+"F24.opExtrude","SWEPT_FACE",FACE,{"disambiguationData":[OSD([sQuery(id+"F23.wireOp",EDGE,"E45.top")])]})],"blendedInto":[makeQuery(id+"F24.opExtrude","SWEPT_FACE",FACE,{"disambiguationData":[OSD([sQuery(id+"F23.wireOp",EDGE,"E45.top")])]})]});
            var Q31;
            Q31=makeQuery(id+"F25.opFillet","BLEND_EDGE",EDGE,{"blendedFrom":[makeQuery(id+"F24.opExtrude","CAP_EDGE",EDGE,{"disambiguationData":[OSD([sQuery(id+"F23.wireOp",EDGE,"E45.left")])],"isStart":false}),makeQuery(id+"F24.opExtrude","SWEPT_FACE",FACE,{"disambiguationData":[OSD([sQuery(id+"F23.wireOp",EDGE,"E45.top")])]})],"blendedInto":[makeQuery(id+"F24.opExtrude","SWEPT_FACE",FACE,{"disambiguationData":[OSD([sQuery(id+"F23.wireOp",EDGE,"E45.top")])]})]});
            var Q32;
            Q32=makeQuery(id+"F22.opFillet","BLEND_EDGE",EDGE,{"blendedFrom":[makeQuery(id+"F21.opExtrude","CAP_EDGE",EDGE,{"disambiguationData":[OSD([sQuery(id+"F20.wireOp",EDGE,"E44.right")])],"isStart":false}),makeQuery(id+"F21.opExtrude","SWEPT_FACE",FACE,{"disambiguationData":[OSD([sQuery(id+"F20.wireOp",EDGE,"E44.top")])]})],"blendedInto":[makeQuery(id+"F21.opExtrude","SWEPT_FACE",FACE,{"disambiguationData":[OSD([sQuery(id+"F20.wireOp",EDGE,"E44.top")])]})]});
            var Q33;
            Q33=makeQuery(id+"F22.opFillet","BLEND_EDGE",EDGE,{"blendedFrom":[makeQuery(id+"F21.opExtrude","CAP_EDGE",EDGE,{"disambiguationData":[OSD([sQuery(id+"F20.wireOp",EDGE,"E44.left")])],"isStart":false}),makeQuery(id+"F21.opExtrude","SWEPT_FACE",FACE,{"disambiguationData":[OSD([sQuery(id+"F20.wireOp",EDGE,"E44.top")])]})],"blendedInto":[makeQuery(id+"F21.opExtrude","SWEPT_FACE",FACE,{"disambiguationData":[OSD([sQuery(id+"F20.wireOp",EDGE,"E44.top")])]})]});
            var Q34;
            Q34=makeQuery(id+"F13.opFillet","BLEND_EDGE",EDGE,{"blendedFrom":[makeQuery(id+"F12.opExtrude","CAP_EDGE",EDGE,{"disambiguationData":[OSD([sQuery(id+"F11.wireOp",EDGE,"E41.left")])],"isStart":false}),makeQuery(id+"F12.opExtrude","SWEPT_FACE",FACE,{"disambiguationData":[OSD([sQuery(id+"F11.wireOp",EDGE,"E41.top")])]})],"blendedInto":[makeQuery(id+"F12.opExtrude","SWEPT_FACE",FACE,{"disambiguationData":[OSD([sQuery(id+"F11.wireOp",EDGE,"E41.top")])]})]});
            var Q35;
            Q35=makeQuery(id+"F13.opFillet","BLEND_EDGE",EDGE,{"blendedFrom":[makeQuery(id+"F12.opExtrude","CAP_EDGE",EDGE,{"disambiguationData":[OSD([sQuery(id+"F11.wireOp",EDGE,"E41.right")])],"isStart":false}),makeQuery(id+"F12.opExtrude","SWEPT_FACE",FACE,{"disambiguationData":[OSD([sQuery(id+"F11.wireOp",EDGE,"E41.top")])]})],"blendedInto":[makeQuery(id+"F12.opExtrude","SWEPT_FACE",FACE,{"disambiguationData":[OSD([sQuery(id+"F11.wireOp",EDGE,"E41.top")])]})]});
            fillet(context, id + "F32", {"entities" : qUnion([Q0, Q1, Q2, Q3, Q4, Q5, Q6, Q7, Q8, Q9, Q10, Q11, Q12, Q13, Q14, Q15, Q16, Q17, Q18, Q19, Q20, Q21, Q22, Q23, Q24, Q25, Q26, Q27, Q28, Q29, Q30, Q31, Q32, Q33, Q34, Q35]), "radius" : 0.4 * mm, "tangentPropagation" : true, "allowEdgeOverflow" : false});
        }
    });
